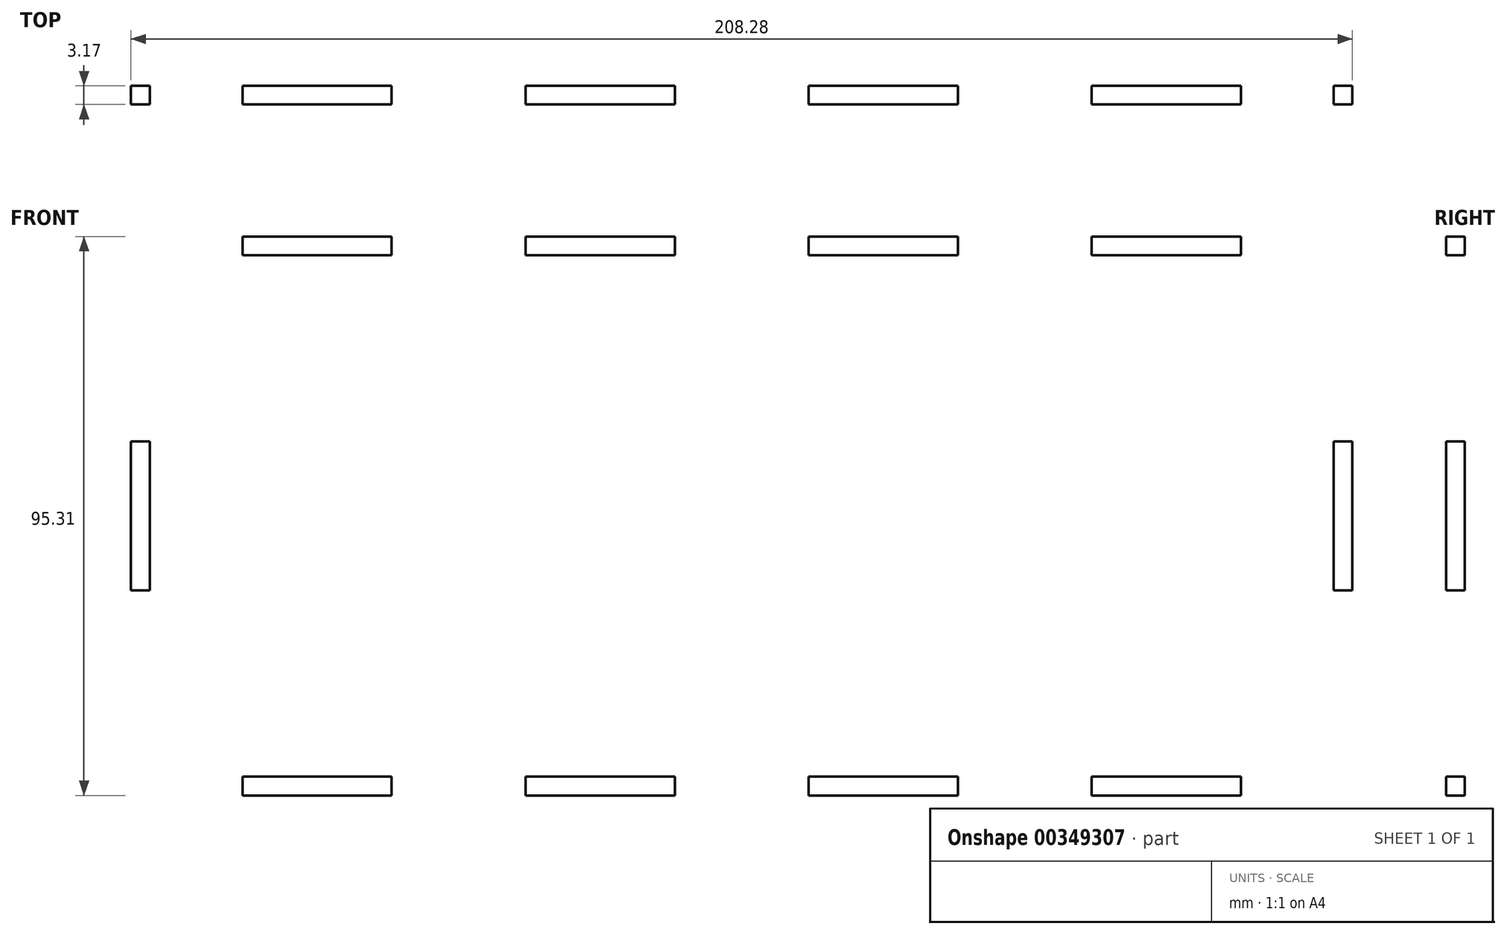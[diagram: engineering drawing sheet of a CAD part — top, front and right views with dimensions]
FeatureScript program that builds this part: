
annotation { "Feature Type Name" : "Feature", "Feature Type Description" : "" }
export const myFeature = defineFeature(function(context is Context, id is Id, definition is map)
    precondition{}
    {
        {
            var Q0;
            Q0=qCreatedBy(makeId("Front.planeOp"),FACE);
            var sketch = newSketch(context, id + "F0", { "sketchPlane" : qUnion([Q0])});
            skLineSegment(sketch, "E0.bottom", {"start": v(-85.62, 42.15) * mm, "end": v(116.26, 42.15) * mm});
            skLineSegment(sketch, "E0.top", {"start": v(-85.62, -46.75) * mm, "end": v(116.26, -46.75) * mm});
            skLineSegment(sketch, "E1.bottom", {"start": v(-69.8, 42.15) * mm, "end": v(-44.36, 42.15) * mm});
            skLineSegment(sketch, "E1.top", {"start": v(-69.8, 45.36) * mm, "end": v(-44.36, 45.36) * mm});
            skLineSegment(sketch, "E1.left", {"start": v(-69.8, 42.15) * mm, "end": v(-69.8, 45.36) * mm});
            skLineSegment(sketch, "E1.right", {"start": v(-44.36, 42.15) * mm, "end": v(-44.36, 45.36) * mm});
            skLineSegment(sketch, "E2.bottom", {"start": v(-21.52, 42.15) * mm, "end": v(3.9, 42.15) * mm});
            skLineSegment(sketch, "E2.top", {"start": v(-21.52, 45.36) * mm, "end": v(3.9, 45.36) * mm});
            skLineSegment(sketch, "E2.left", {"start": v(-21.52, 42.15) * mm, "end": v(-21.52, 45.36) * mm});
            skLineSegment(sketch, "E2.right", {"start": v(3.9, 42.15) * mm, "end": v(3.9, 45.36) * mm});
            skLineSegment(sketch, "E3.bottom", {"start": v(26.75, 42.15) * mm, "end": v(52.17, 42.15) * mm});
            skLineSegment(sketch, "E3.top", {"start": v(26.75, 45.36) * mm, "end": v(52.17, 45.36) * mm});
            skLineSegment(sketch, "E3.left", {"start": v(26.75, 42.15) * mm, "end": v(26.75, 45.36) * mm});
            skLineSegment(sketch, "E3.right", {"start": v(52.17, 42.15) * mm, "end": v(52.17, 45.36) * mm});
            skLineSegment(sketch, "E4.bottom", {"start": v(75.01, 42.15) * mm, "end": v(100.44, 42.15) * mm});
            skLineSegment(sketch, "E4.top", {"start": v(75.01, 45.36) * mm, "end": v(100.44, 45.36) * mm});
            skLineSegment(sketch, "E4.left", {"start": v(75.01, 42.15) * mm, "end": v(75.01, 45.36) * mm});
            skLineSegment(sketch, "E4.right", {"start": v(100.44, 42.15) * mm, "end": v(100.44, 45.36) * mm});
            skLineSegment(sketch, "E5.bottom", {"start": v(-69.8, -46.75) * mm, "end": v(-44.37, -46.75) * mm});
            skLineSegment(sketch, "E5.top", {"start": v(-69.8, -49.95) * mm, "end": v(-44.37, -49.95) * mm});
            skLineSegment(sketch, "E5.left", {"start": v(-69.8, -46.75) * mm, "end": v(-69.8, -49.95) * mm});
            skLineSegment(sketch, "E5.right", {"start": v(-44.37, -46.75) * mm, "end": v(-44.37, -49.95) * mm});
            skLineSegment(sketch, "E6.bottom", {"start": v(-21.52, -46.75) * mm, "end": v(3.9, -46.75) * mm});
            skLineSegment(sketch, "E6.top", {"start": v(-21.52, -49.95) * mm, "end": v(3.9, -49.95) * mm});
            skLineSegment(sketch, "E6.left", {"start": v(-21.52, -46.75) * mm, "end": v(-21.52, -49.95) * mm});
            skLineSegment(sketch, "E6.right", {"start": v(3.9, -46.75) * mm, "end": v(3.9, -49.95) * mm});
            skLineSegment(sketch, "E7.bottom", {"start": v(26.75, -46.75) * mm, "end": v(52.17, -46.75) * mm});
            skLineSegment(sketch, "E7.top", {"start": v(26.75, -49.95) * mm, "end": v(52.17, -49.95) * mm});
            skLineSegment(sketch, "E7.left", {"start": v(26.75, -46.75) * mm, "end": v(26.75, -49.95) * mm});
            skLineSegment(sketch, "E7.right", {"start": v(52.17, -46.75) * mm, "end": v(52.17, -49.95) * mm});
            skLineSegment(sketch, "E8.bottom", {"start": v(75.01, -46.75) * mm, "end": v(100.44, -46.75) * mm});
            skLineSegment(sketch, "E8.top", {"start": v(75.01, -49.95) * mm, "end": v(100.44, -49.95) * mm});
            skLineSegment(sketch, "E8.left", {"start": v(75.01, -46.75) * mm, "end": v(75.01, -49.95) * mm});
            skLineSegment(sketch, "E8.right", {"start": v(100.44, -46.75) * mm, "end": v(100.44, -49.95) * mm});
            skLineSegment(sketch, "E9.left", {"start": v(-85.62, 42.15) * mm, "end": v(-85.62, -46.75) * mm});
            skLineSegment(sketch, "E9.right", {"start": v(116.26, 42.15) * mm, "end": v(116.26, -46.75) * mm});
            skLineSegment(sketch, "E10.bottom", {"start": v(-85.62, -15) * mm, "end": v(-88.82, -15) * mm});
            skLineSegment(sketch, "E10.top", {"start": v(-85.62, 10.42) * mm, "end": v(-88.82, 10.42) * mm});
            skLineSegment(sketch, "E10.left", {"start": v(-85.62, -15) * mm, "end": v(-85.62, 10.42) * mm});
            skLineSegment(sketch, "E10.right", {"start": v(-88.82, -15) * mm, "end": v(-88.82, 10.42) * mm});
            skPoint(sketch, "E11", {"position": v(-85.62, -2.3) * mm});
            skPoint(sketch, "E12", {"position": v(116.26, -2.3) * mm});
            skLineSegment(sketch, "E13.bottom", {"start": v(116.26, 10.42) * mm, "end": v(119.46, 10.42) * mm});
            skLineSegment(sketch, "E13.top", {"start": v(116.26, -15) * mm, "end": v(119.46, -15) * mm});
            skLineSegment(sketch, "E13.left", {"start": v(116.26, 10.42) * mm, "end": v(116.26, -15) * mm});
            skLineSegment(sketch, "E13.right", {"start": v(119.46, 10.42) * mm, "end": v(119.46, -15) * mm});
            skSolve(sketch);
        }
        {
            var Q0;
            Q0=makeQuery(id+"F0.imprint","IMPRINT",FACE,{"disambiguationData":[TD([[makeQuery(id+"F0.imprint","IMPRINT",EDGE,{"derivedFrom":sQuery(id+"F0.wireOp",EDGE,"E10.bottom")}),-1.0]])]});
            var Q1;
            Q1=makeQuery(id+"F0.imprint","IMPRINT",FACE,{"disambiguationData":[TD([[makeQuery(id+"F0.imprint","IMPRINT",EDGE,{"derivedFrom":sQuery(id+"F0.wireOp",EDGE,"E1.top")}),-1.0]])]});
            var Q2;
            {var subQ8=sQuery(id+"F0.wireOp",EDGE,"E10.left");Q2=makeQuery(id+"F0.imprint","IMPRINT",FACE,{"disambiguationData":[TD([[makeQuery(id+"F0.imprint","IMPRINT",EDGE,{"derivedFrom":subQ8}),-1.0]])]});}
            var Q3;
            Q3=makeQuery(id+"F0.imprint","IMPRINT",FACE,{"disambiguationData":[TD([[makeQuery(id+"F0.imprint","IMPRINT",EDGE,{"derivedFrom":sQuery(id+"F0.wireOp",EDGE,"E3.top")}),-1.0]])]});
            var Q4;
            Q4=makeQuery(id+"F0.imprint","IMPRINT",FACE,{"disambiguationData":[TD([[makeQuery(id+"F0.imprint","IMPRINT",EDGE,{"derivedFrom":sQuery(id+"F0.wireOp",EDGE,"E4.top")}),-1.0]])]});
            var Q5;
            Q5=makeQuery(id+"F0.imprint","IMPRINT",FACE,{"disambiguationData":[TD([[makeQuery(id+"F0.imprint","IMPRINT",EDGE,{"derivedFrom":sQuery(id+"F0.wireOp",EDGE,"E13.bottom")}),-1.0]])]});
            var Q6;
            Q6=makeQuery(id+"F0.imprint","IMPRINT",FACE,{"disambiguationData":[TD([[makeQuery(id+"F0.imprint","IMPRINT",EDGE,{"derivedFrom":sQuery(id+"F0.wireOp",EDGE,"E8.top")}),1.0]])]});
            var Q7;
            Q7=makeQuery(id+"F0.imprint","IMPRINT",FACE,{"disambiguationData":[TD([[makeQuery(id+"F0.imprint","IMPRINT",EDGE,{"derivedFrom":sQuery(id+"F0.wireOp",EDGE,"E7.top")}),1.0]])]});
            var Q8;
            Q8=makeQuery(id+"F0.imprint","IMPRINT",FACE,{"disambiguationData":[TD([[makeQuery(id+"F0.imprint","IMPRINT",EDGE,{"derivedFrom":sQuery(id+"F0.wireOp",EDGE,"E6.top")}),1.0]])]});
            var Q9;
            Q9=makeQuery(id+"F0.imprint","IMPRINT",FACE,{"disambiguationData":[TD([[makeQuery(id+"F0.imprint","IMPRINT",EDGE,{"derivedFrom":sQuery(id+"F0.wireOp",EDGE,"E5.top")}),1.0]])]});
            var Q10;
            Q10=makeQuery(id+"F0.imprint","IMPRINT",FACE,{"disambiguationData":[TD([[makeQuery(id+"F0.imprint","IMPRINT",EDGE,{"derivedFrom":sQuery(id+"F0.wireOp",EDGE,"E2.top")}),-1.0]])]});
            extrude(context, id + "F1", {"entities" : qUnion([Q0, Q1, Q2, Q3, Q4, Q5, Q6, Q7, Q8, Q9, Q10]), "depth" : 3.17 * mm});
        }
    });
